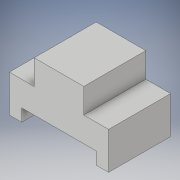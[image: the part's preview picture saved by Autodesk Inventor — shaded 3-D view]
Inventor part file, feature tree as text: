
AUTODESK INVENTOR PART (.ipt)
format: ipt  version: 2017 (Build 210142000, 142)  size: 101,376 bytes
history: native  units: in
note: dims shown in document units (in); Inventor stores cm internally (conversion verified against a paired STEP export)
features: extrude x1, sketch x1
ambient origin geometry x8: Origin, YZ Plane, XZ Plane, XY Plane, X Axis, Y Axis, Z Axis, Center Point
bodies: Solid1 (feature_tree)
feature tree (2):
  extrude  "Extrusion1"  Depth=0.25in
  sketch  "Sketch1"  dims[d1=0.25in d2=0.25in d3=1.5in d4=0.25in d5=0.75in d6=0.5in d7=0.5in d8=1.0in d9=1.25in d10=0.0in]
